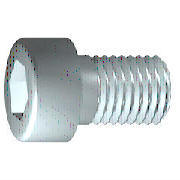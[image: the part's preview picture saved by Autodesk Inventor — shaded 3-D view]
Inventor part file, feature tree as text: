
AUTODESK INVENTOR PART (.ipt)
format: ipt  version: 2020 (Build 240168000, 168)  size: 188,928 bytes
history: native  units: mm (DEFAULTED — no unit token found)
features: sketch x2, extrude x1, plane x1, fillet x1
ambient origin geometry x7: Origin, YZ Plane, XY Plane, X Axis, Y Axis, Z Axis, Center Point
bodies: Solid1 (feature_tree), Body (feature_tree)
feature tree (5):
  extrude  "Slot"  Depth=6.0mm
  plane  "Work Plane1"
  fillet  "Fillet2"  Radius=6.0mm
  sketch  "Sketch1"  dims[d1=24.0mm d2=0.61355mm d3=6.0mm]
  sketch  "Sketch2"  dims[d4=3.0mm d5=60.0deg d6=6.0mm d7=6.0mm d8=5.773503mm d9=10.0mm d10=90.0deg d11=10.0mm d12=0.0mm d13=24.0mm d14=0.0mm d15=0.61345mm d16=0.61345mm d17=0.6mm d19=0.0mm d26=55.0mm d27=45.0deg d28=0.0mm d29=0.0mm d30=0.25mm]
